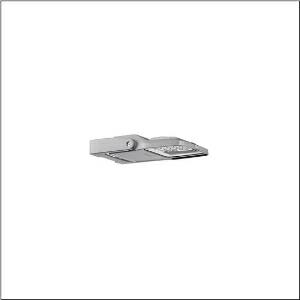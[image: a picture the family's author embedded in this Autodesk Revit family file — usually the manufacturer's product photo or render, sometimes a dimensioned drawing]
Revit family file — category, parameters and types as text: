
# Revit family: floodlight_fl_21_micro___pl43_5xa7762a4a2a_8d9f
name_source: partatom
category: Lighting Fixtures
units: mm (PartAtom-declared; Revit-internal decimal feet)

## family parameters
Cut with Voids When Loaded = No
Host = Face
Light Source = No
Part Type = Normal
Room Calculation Point = No
Round Connector Dimension = Use Diameter
Shared = No

## types (1)
- --- (1 x LED, 3170 lm, 23.1 W, 4000K)
    Apparent Load = 23 VA
    CIE Flux Codes = 29 80 99 100 100
    Color Rendering = 70
    Color Temperature = 4000K
    Default Elevation = 1800 mm
    Description = Floodlight FL 21 micro, floodlight, primary light control with lens, of PMMA, primary optical cover: protective disc, of toughened safety glass, transparent, light distribution: PL43, light emission: direct distribution, installation type: surface-mounted, LED, High Power LED, rated luminous flux: 3.170lm, luminous efficacy: 137lm/W, light colour: 740, colour temperature: 4000K, control gear: ECG iQ, control: Auto-Match, Temp-Guard, Night-Set, Smart-Wire, Desk-Remote (wireless, voltage-free reading and setting of iQ features in the workshop via application-optimized NFC function/RFID function), optimised constant luminous flux control (CLO 2.0), Street-Remote, with terminal, 6-pole, mains connection: 220..240V, AC, 50/60Hz, start of lifetime: 23W, end of lifetime: 24W, reduction: 11W, luminaire housing, of diecast aluminium, powder-coated, Siteco® metallic grey (DB 702S), corrosivity category C5 according to DIN EN ISO 12944, design bracket, of diecast aluminium, powder-coated, Siteco® metallic grey (DB 702S), protection rating (complete): IP66, insulation class (complete): insulation class II (safety insulation), certification: CE, protection symbol: D, impact resistance: IK07, permissible operating ambient temperature: -40..+40°C, permissible operating ambient temperature for outdoor applications: -40..+50°C, standard: DIN EN 12944, packaging unit: 1 piece

Light Distribution: PL43
    Height = 65 mm
    Lamp = 1 x LED
    Lamp Light Flux = 3170 lm
    Lamp Power = 23.1 W
    Lamp count = 1
    Length = 312 mm
    Luminous efficacy = 137 lm/W
    Manufacturer = Siteco
    ModVariant = No
    Model = 5XA7762A4A2A
    Number of Poles = 1
    OnlyDefault = Yes
    Power Factor = 1
    Product Name = Floodlight FL 21 micro | PL43
    Product group = floodlight | pylon top
    ProductGroupID = 6101
    Protection Class = Protection class II
    Protection Degree = IP 66
    RLX_Detail_Level = 1
    RlxData = <blob elided: 97337 chars, md5=68c89c48>
    Socket = socket
    Standby Power = 0 W
    System Light Flux = 3170 lm
    System Power = 23 W
    Type Comments = factory setting: luminous flux: 100 % | dim-lin: 254 | 455 mA
    Type Image = l_1006878.jpg
    URL = http://relux.com
    VarID = @adj_089785
    Voltage = 0 V
    Weight = 0.00 kg
    Width = 230 mm

## geometry (parser evidence)
native form markers: Blend x4, Sweep x12
no freeform markers — native parametric forms only
